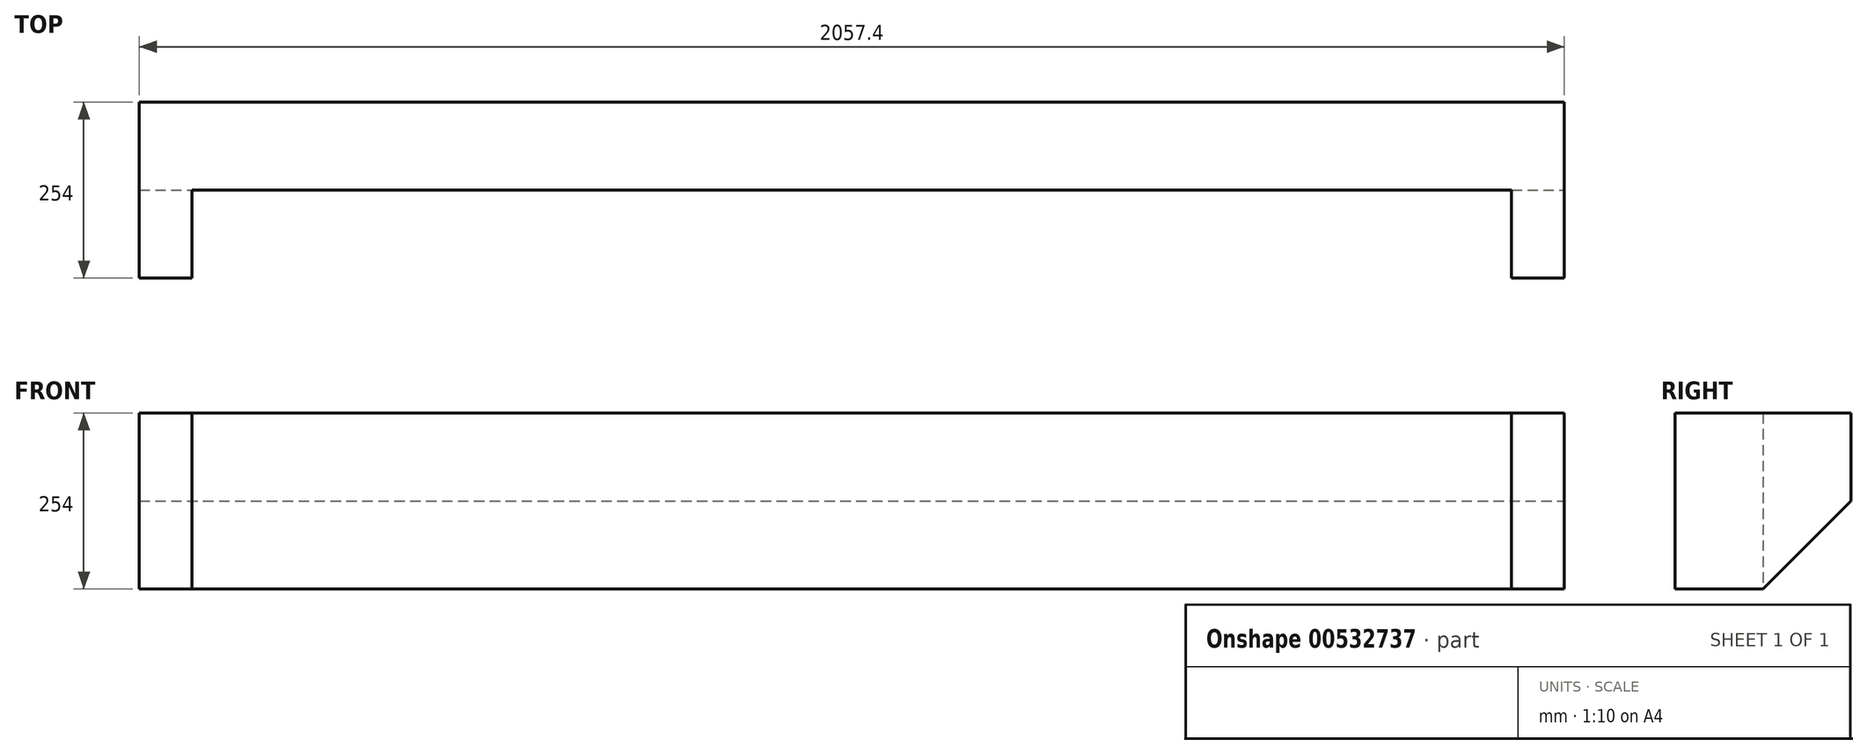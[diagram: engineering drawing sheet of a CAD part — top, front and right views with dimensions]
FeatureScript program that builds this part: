
annotation { "Feature Type Name" : "Feature", "Feature Type Description" : "" }
export const myFeature = defineFeature(function(context is Context, id is Id, definition is map)
    precondition{}
    {
        {
            var Q0;
            Q0=qCreatedBy(makeId("Top.planeOp"),FACE);
            var sketch = newSketch(context, id + "F0", { "sketchPlane" : qUnion([Q0])});
            skLineSegment(sketch, "E0", {"start": v(0, 0) * mm, "end": v(1905, 0) * mm});
            skLineSegment(sketch, "E1", {"start": v(1905, 0) * mm, "end": v(1905, -127) * mm});
            skLineSegment(sketch, "E2", {"start": v(1905, -127) * mm, "end": v(1981.2, -127) * mm});
            skLineSegment(sketch, "E3", {"start": v(1981.2, -127) * mm, "end": v(1981.2, 127) * mm});
            skLineSegment(sketch, "E4", {"start": v(1981.2, 127) * mm, "end": v(-76.2, 127) * mm});
            skLineSegment(sketch, "E5", {"start": v(-76.2, 127) * mm, "end": v(-76.2, -127) * mm});
            skLineSegment(sketch, "E6", {"start": v(-76.2, -127) * mm, "end": v(0, -127) * mm});
            skLineSegment(sketch, "E7", {"start": v(0, -127) * mm, "end": v(0, 0) * mm});
            skSolve(sketch);
        }
        {
            var Q0;
            Q0 = qSketchRegion(id + "F0", true);
            extrude(context, id + "F1", {"entities" : qUnion([Q0]), "depth" : 254 * mm, "offsetDistance" : 25.4 * mm});
        }
        {
            var Q0;
            Q0=makeQuery(id+"F1.opExtrude","SWEPT_FACE",FACE,{"disambiguationData":[OSD([sQuery(id+"F0.wireOp",EDGE,"E3")])]});
            var sketch = newSketch(context, id + "F2", { "sketchPlane" : qUnion([Q0])});
            skLineSegment(sketch, "E8", {"start": v(0, 0) * mm, "end": v(127, 127) * mm});
            skSolve(sketch);
        }
        {
            var Q0;
            {var subQ0=sQuery(id+"F2.wireOp",EDGE,"E8");Q0=makeQuery(id+"F2.imprint","IMPRINT",FACE,{"disambiguationData":[TD([[makeQuery(id+"F2.imprint","IMPRINT",EDGE,{"derivedFrom":subQ0}),-1.0]])]});}
            extrude(context, id + "F3", {"entities" : qUnion([Q0]), "operationType" : NewBodyOperationType.REMOVE, "oppositeDirection" : true, "depth" : 2057.4 * mm, "offsetDistance" : 25.4 * mm});
        }
    });
